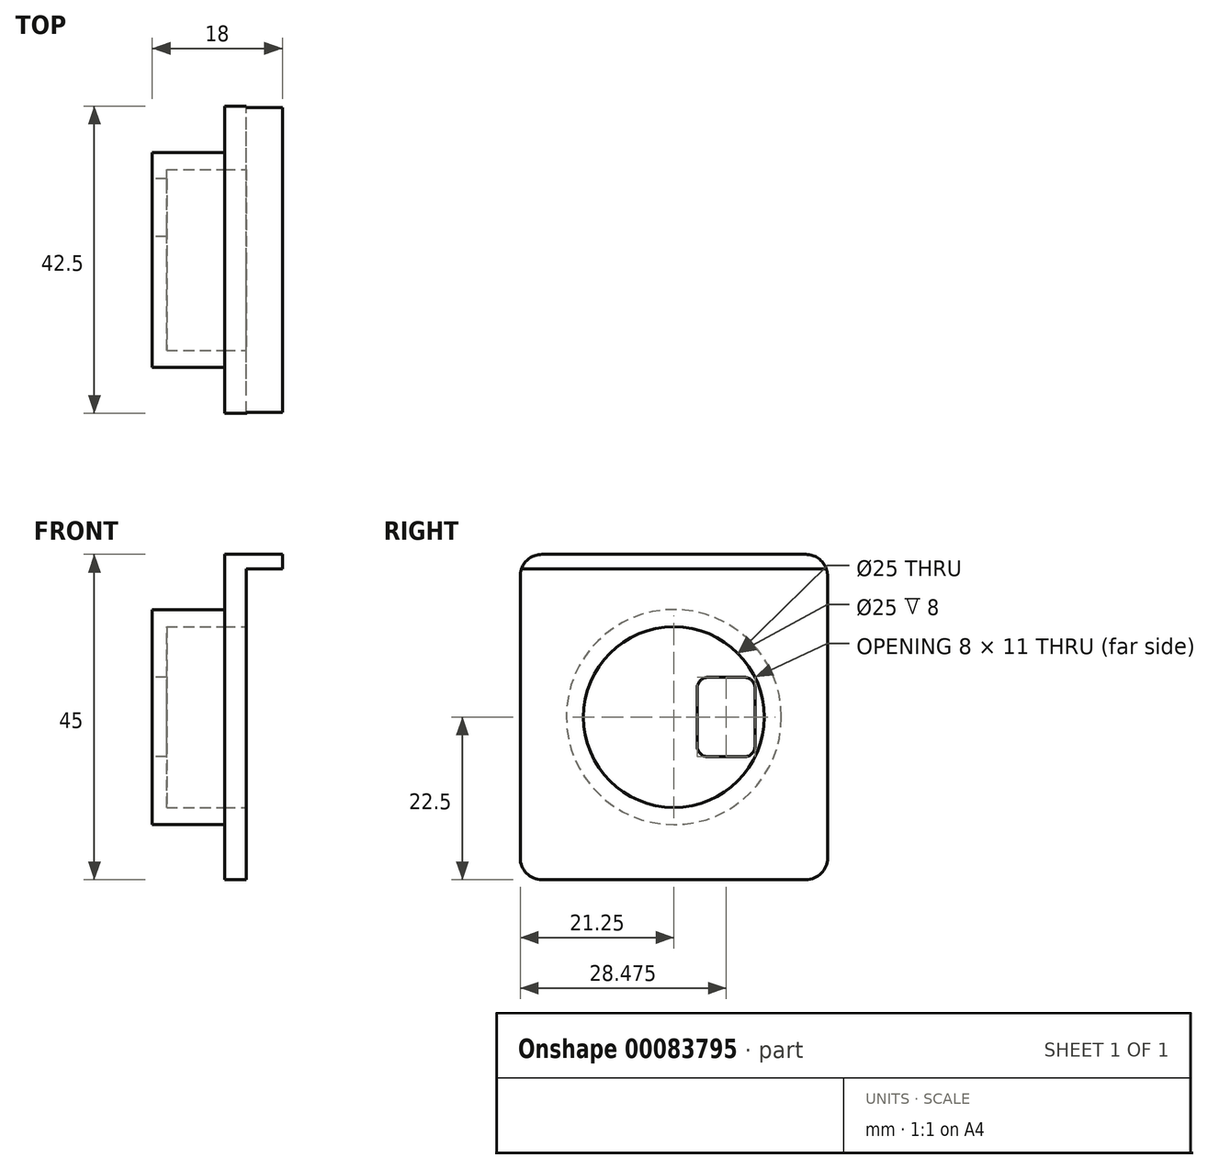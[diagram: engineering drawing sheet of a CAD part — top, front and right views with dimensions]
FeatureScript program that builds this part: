
annotation { "Feature Type Name" : "Feature", "Feature Type Description" : "" }
export const myFeature = defineFeature(function(context is Context, id is Id, definition is map)
    precondition{}
    {
        {
            var Q0;
            Q0=qCreatedBy(makeId("Right.planeOp"),FACE);
            var sketch = newSketch(context, id + "F0", { "sketchPlane" : qUnion([Q0])});
            skCircle(sketch, "E0", {"center": v(0, 0) * mm, "radius": 14.88 * mm});
            skSolve(sketch);
        }
        {
            var Q0;
            Q0 = qSketchRegion(id + "F0", true);
            extrude(context, id + "F1", {"entities" : qUnion([Q0]), "depth" : 10 * mm});
        }
        {
            var Q0;
            Q0=makeQuery(id+"F1.opExtrude","CAP_FACE",FACE,{"disambiguationData":[OSD([sQuery(id+"F0.wireOp",EDGE,"E0")])],"isStart":false});
            var sketch = newSketch(context, id + "F2", { "sketchPlane" : qUnion([Q0])});
            skLineSegment(sketch, "E1.bottom", {"start": v(-21.25, 22.5) * mm, "end": v(21.25, 22.5) * mm});
            skLineSegment(sketch, "E1.top", {"start": v(-21.25, -22.5) * mm, "end": v(21.25, -22.5) * mm});
            skLineSegment(sketch, "E1.left", {"start": v(-21.25, 22.5) * mm, "end": v(-21.25, -22.5) * mm});
            skLineSegment(sketch, "E1.right", {"start": v(21.25, 22.5) * mm, "end": v(21.25, -22.5) * mm});
            skPoint(sketch, "E2", {"position": v(0, 22.5) * mm});
            skPoint(sketch, "E3", {"position": v(21.25, 0) * mm});
            skSolve(sketch);
        }
        {
            var Q0;
            Q0=makeQuery(id+"F2.imprint","IMPRINT",FACE,{"disambiguationData":[TD([[makeQuery(id+"F2.imprint","IMPRINT",EDGE,{"derivedFrom":sQuery(id+"F2.wireOp",EDGE,"E1.bottom")}),-1.0]])]});
            var Q1;
            Q1=makeQuery(id+"F2.imprint","IMPRINT",FACE,{"disambiguationData":[TD([[makeQuery(id+"F2.imprint","IMPRINT",EDGE,{"derivedFrom":makeQuery(id+"F1.opExtrude","CAP_EDGE",EDGE,{"disambiguationData":[OSD([sQuery(id+"F0.wireOp",EDGE,"E0")])],"isStart":false})}),1.0]])]});
            extrude(context, id + "F3", {"entities" : qUnion([Q0, Q1]), "depth" : 3 * mm});
        }
        {
            var Q0;
            Q0=makeQuery(id+"F3.opExtrude","CAP_FACE",FACE,{"disambiguationData":[OSD([sQuery(id+"F2.wireOp",EDGE,"E1.bottom"),sQuery(id+"F2.wireOp",EDGE,"E1.top"),sQuery(id+"F2.wireOp",EDGE,"E1.left"),sQuery(id+"F2.wireOp",EDGE,"E1.right")])],"isStart":false});
            var sketch = newSketch(context, id + "F4", { "sketchPlane" : qUnion([Q0])});
            skCircle(sketch, "E4", {"center": v(0, 0) * mm, "radius": 12.5 * mm});
            skSolve(sketch);
        }
        {
            var Q0;
            Q0 = qSketchRegion(id + "F4", true);
            extrude(context, id + "F5", {"entities" : qUnion([Q0]), "operationType" : NewBodyOperationType.REMOVE, "oppositeDirection" : true, "depth" : 11 * mm});
        }
        {
            var Q0;
            Q0=makeQuery(id+"F1.opExtrude","CAP_FACE",FACE,{"disambiguationData":[OSD([sQuery(id+"F0.wireOp",EDGE,"E0")])],"isStart":true});
            var sketch = newSketch(context, id + "F6", { "sketchPlane" : qUnion([Q0])});
            skLineSegment(sketch, "E5.bottom", {"start": v(-11.22, 5.5) * mm, "end": v(-3.22, 5.5) * mm});
            skLineSegment(sketch, "E5.top", {"start": v(-11.22, -5.5) * mm, "end": v(-3.22, -5.5) * mm});
            skLineSegment(sketch, "E5.left", {"start": v(-11.22, 5.5) * mm, "end": v(-11.22, -5.5) * mm});
            skLineSegment(sketch, "E5.right", {"start": v(-3.22, 5.5) * mm, "end": v(-3.22, -5.5) * mm});
            skLineSegment(sketch, "E6", {"start": v(-14.88, 0) * mm, "end": v(14.88, 0) * mm, "construction": true});
            skSolve(sketch);
        }
        {
            var Q0;
            Q0=makeQuery(id+"F6.imprint","IMPRINT",FACE,{"disambiguationData":[TD([[makeQuery(id+"F6.imprint","IMPRINT",EDGE,{"derivedFrom":sQuery(id+"F6.wireOp",EDGE,"E5.bottom")}),-1.0]])]});
            extrude(context, id + "F7", {"entities" : qUnion([Q0]), "operationType" : NewBodyOperationType.REMOVE, "endBound" : BoundingType.THROUGH_ALL, "oppositeDirection" : true, "depth" : 25 * mm});
        }
        {
            var Q0;
            Q0=makeQuery(id+"F3.opExtrude","CAP_FACE",FACE,{"disambiguationData":[OSD([sQuery(id+"F2.wireOp",EDGE,"E1.bottom"),sQuery(id+"F2.wireOp",EDGE,"E1.top"),sQuery(id+"F2.wireOp",EDGE,"E1.left"),sQuery(id+"F2.wireOp",EDGE,"E1.right")])],"isStart":false});
            var sketch = newSketch(context, id + "F8", { "sketchPlane" : qUnion([Q0])});
            skLineSegment(sketch, "E7.bottom", {"start": v(-21.25, 22.5) * mm, "end": v(21.25, 22.5) * mm});
            skLineSegment(sketch, "E7.top", {"start": v(-21.25, 20.5) * mm, "end": v(21.25, 20.5) * mm});
            skLineSegment(sketch, "E7.left", {"start": v(-21.25, 22.5) * mm, "end": v(-21.25, 20.5) * mm});
            skLineSegment(sketch, "E7.right", {"start": v(21.25, 22.5) * mm, "end": v(21.25, 20.5) * mm});
            skSolve(sketch);
        }
        {
            var Q0;
            Q0 = qSketchRegion(id + "F8", true);
            extrude(context, id + "F9", {"entities" : qUnion([Q0]), "operationType" : NewBodyOperationType.ADD, "depth" : 5 * mm});
        }
        {
            var Q0;
            Q0=makeQuery(id+"F3.opExtrude","SWEPT_EDGE",EDGE,{"disambiguationData":[OSD([sQuery(id+"F2.wireOp",EDGE,"E1.bottom"),sQuery(id+"F2.wireOp",EDGE,"E1.left")])]});
            var Q1;
            Q1=makeQuery(id+"F3.opExtrude","SWEPT_EDGE",EDGE,{"disambiguationData":[OSD([sQuery(id+"F2.wireOp",EDGE,"E1.top"),sQuery(id+"F2.wireOp",EDGE,"E1.left")])]});
            var Q2;
            Q2=makeQuery(id+"F3.opExtrude","SWEPT_EDGE",EDGE,{"disambiguationData":[OSD([sQuery(id+"F2.wireOp",EDGE,"E1.bottom"),sQuery(id+"F2.wireOp",EDGE,"E1.right")])]});
            var Q3;
            Q3=makeQuery(id+"F3.opExtrude","SWEPT_EDGE",EDGE,{"disambiguationData":[OSD([sQuery(id+"F2.wireOp",EDGE,"E1.top"),sQuery(id+"F2.wireOp",EDGE,"E1.right")])]});
            fillet(context, id + "F10", {"entities" : qUnion([Q0, Q1, Q2, Q3]), "radius" : 3 * mm, "tangentPropagation" : true, "allowEdgeOverflow" : false});
        }
        {
            var Q0;
            Q0=makeQuery(id+"F7.boolean.opBoolean","COPY",EDGE,{"derivedFrom":makeQuery(id+"F7.opExtrude","SWEPT_EDGE",EDGE,{"disambiguationData":[OSD([sQuery(id+"F6.wireOp",EDGE,"E5.bottom"),sQuery(id+"F6.wireOp",EDGE,"E5.left")])]})});
            var Q1;
            Q1=makeQuery(id+"F7.boolean.opBoolean","COPY",EDGE,{"derivedFrom":makeQuery(id+"F7.opExtrude","SWEPT_EDGE",EDGE,{"disambiguationData":[OSD([sQuery(id+"F6.wireOp",EDGE,"E5.bottom"),sQuery(id+"F6.wireOp",EDGE,"E5.right")])]})});
            var Q2;
            Q2=makeQuery(id+"F7.boolean.opBoolean","COPY",EDGE,{"derivedFrom":makeQuery(id+"F7.opExtrude","SWEPT_EDGE",EDGE,{"disambiguationData":[OSD([sQuery(id+"F6.wireOp",EDGE,"E5.top"),sQuery(id+"F6.wireOp",EDGE,"E5.right")])]})});
            var Q3;
            Q3=makeQuery(id+"F7.boolean.opBoolean","COPY",EDGE,{"derivedFrom":makeQuery(id+"F7.opExtrude","SWEPT_EDGE",EDGE,{"disambiguationData":[OSD([sQuery(id+"F6.wireOp",EDGE,"E5.top"),sQuery(id+"F6.wireOp",EDGE,"E5.left")])]})});
            fillet(context, id + "F11", {"entities" : qUnion([Q0, Q1, Q2, Q3]), "radius" : 1.5 * mm, "allowEdgeOverflow" : false});
        }
    });
